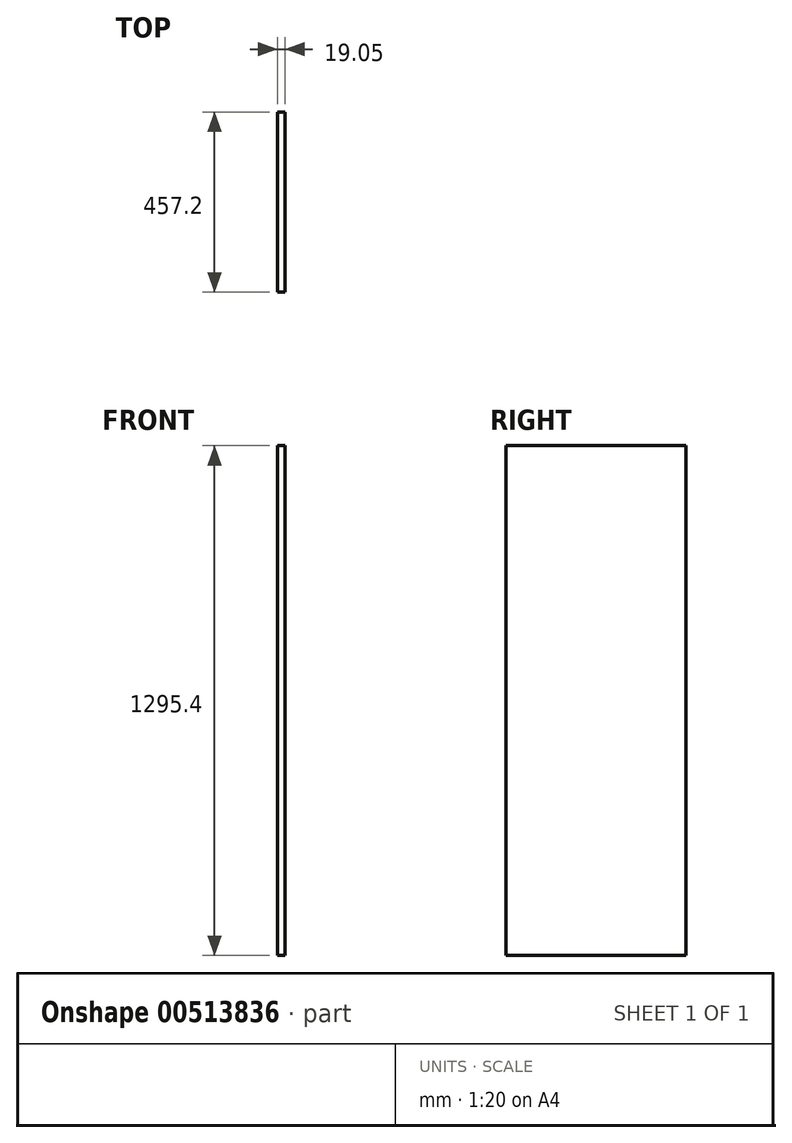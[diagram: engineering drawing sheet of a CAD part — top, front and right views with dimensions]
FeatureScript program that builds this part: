
annotation { "Feature Type Name" : "Feature", "Feature Type Description" : "" }
export const myFeature = defineFeature(function(context is Context, id is Id, definition is map)
    precondition{}
    {
        {
            var Q0;
            Q0=qCreatedBy(makeId("Right.planeOp"),FACE);
            var sketch = newSketch(context, id + "F0", { "sketchPlane" : qUnion([Q0])});
            skLineSegment(sketch, "E0.bottom", {"start": v(228.6, 647.7) * mm, "end": v(-228.6, 647.7) * mm});
            skLineSegment(sketch, "E0.top", {"start": v(228.6, -647.7) * mm, "end": v(-228.6, -647.7) * mm});
            skLineSegment(sketch, "E0.left", {"start": v(228.6, 647.7) * mm, "end": v(228.6, -647.7) * mm});
            skLineSegment(sketch, "E0.right", {"start": v(-228.6, 647.7) * mm, "end": v(-228.6, -647.7) * mm});
            skPoint(sketch, "E0.middle", {"position": v(0, 0) * mm});
            skSolve(sketch);
        }
        {
            var Q0;
            Q0 = qSketchRegion(id + "F0", true);
            extrude(context, id + "F1", {"entities" : qUnion([Q0]), "depth" : 19.05 * mm});
        }
    });
